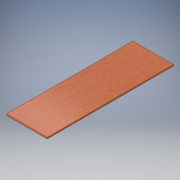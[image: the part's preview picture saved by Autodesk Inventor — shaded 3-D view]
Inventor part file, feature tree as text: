
AUTODESK INVENTOR PART (.ipt)
format: ipt  version: 2018 (Build 220112000, 112)  size: 100,864 bytes
history: native  units: mm
features: extrude x1, sketch x1
ambient origin geometry x8: Origin, YZ Plane, XZ Plane, XY Plane, X Axis, Y Axis, Z Axis, Center Point
bodies: Volumenkörper1 (feature_tree)
feature tree (2):
  extrude  "Extrusion1"  Depth=99.5mm
  sketch  "Skizze1"  dims[d0=32.0mm d1=99.5mm d2=1.2mm d3=0.0mm]
